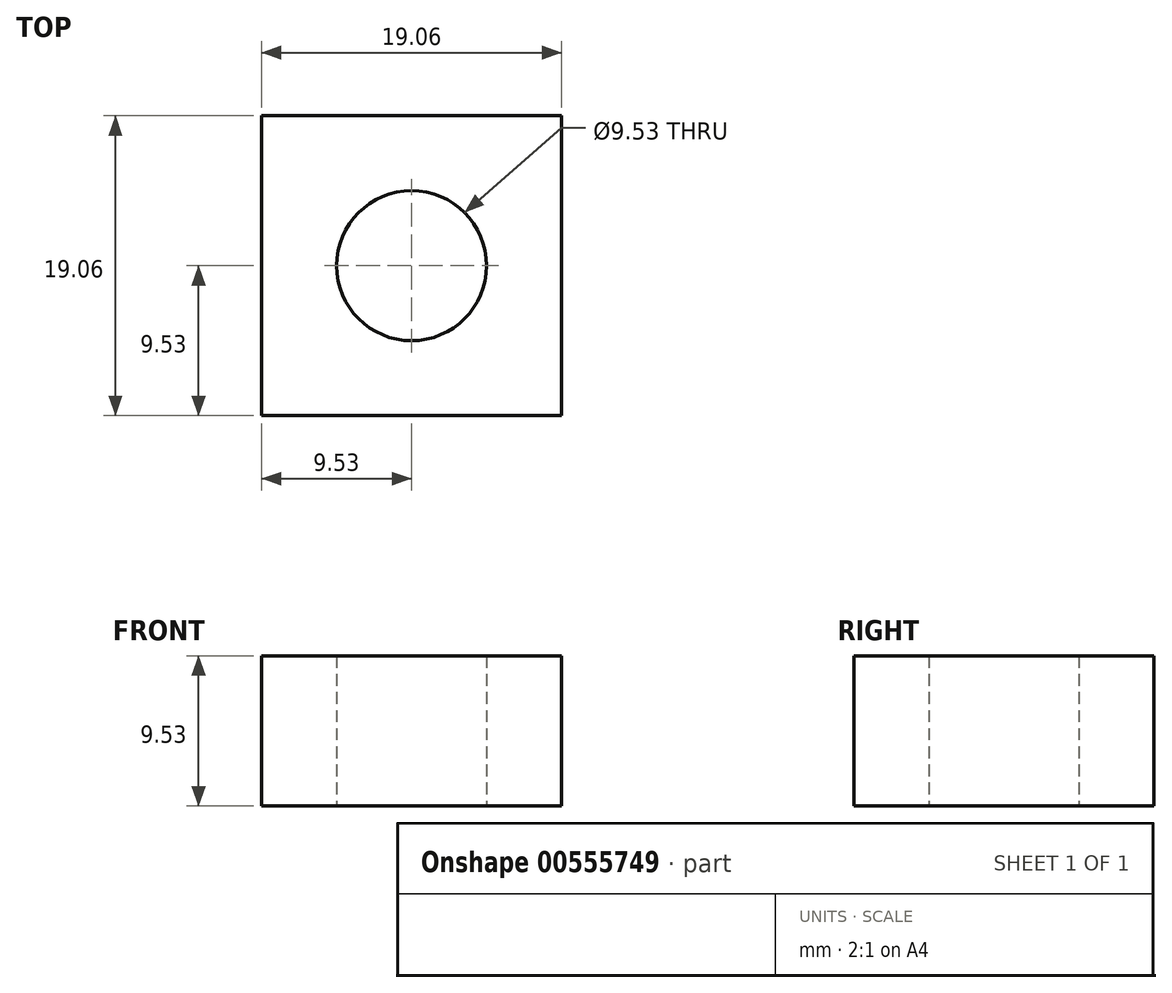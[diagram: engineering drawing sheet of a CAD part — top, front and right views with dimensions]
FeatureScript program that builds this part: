
annotation { "Feature Type Name" : "Feature", "Feature Type Description" : "" }
export const myFeature = defineFeature(function(context is Context, id is Id, definition is map)
    precondition{}
    {
        {
            var Q0;
            Q0=qCreatedBy(makeId("Top.planeOp"),FACE);
            var sketch = newSketch(context, id + "F0", { "sketchPlane" : qUnion([Q0])});
            skCircle(sketch, "E0", {"center": v(0, 0) * mm, "radius": 4.76 * mm});
            skLineSegment(sketch, "E1.bottom", {"start": v(9.52, -9.52) * mm, "end": v(-9.52, -9.53) * mm});
            skLineSegment(sketch, "E1.top", {"start": v(9.53, 9.53) * mm, "end": v(-9.53, 9.52) * mm});
            skLineSegment(sketch, "E1.left", {"start": v(9.53, -9.52) * mm, "end": v(9.53, 9.52) * mm});
            skLineSegment(sketch, "E1.right", {"start": v(-9.53, -9.52) * mm, "end": v(-9.53, 9.52) * mm});
            skSolve(sketch);
        }
        {
            var Q0;
            Q0=makeQuery(id+"F0.imprint","IMPRINT",FACE,{"disambiguationData":[TD([[makeQuery(id+"F0.imprint","IMPRINT",EDGE,{"derivedFrom":sQuery(id+"F0.wireOp",EDGE,"E0")}),-1.0]])]});
            extrude(context, id + "F1", {"entities" : qUnion([Q0]), "depth" : 9.52 * mm, "offsetDistance" : 25.4 * mm});
        }
    });
